# Revit family: 1322xxx Sparta 900 LED 0-10V (UL)
name_source: partatom
category: Lighting Fixtures
revit_build: Autodesk Revit 2018 (Build: 20170223_1515(x64)
units: mm (PartAtom-declared; Revit-internal decimal feet)

## family parameters
Always vertical = Yes
Cut with Voids When Loaded = No
Host = Wall
Light Source = Yes
OmniClass Number = 23.80.70.00
OmniClass Title = Lighting
Part Type = Normal
Room Calculation Point = No
Round Connector Dimension = Use Diameter
Shared = No

## types (1)
- Astro Sparta 900 LED 0-10V
    ADA compliant = Yes
    Color Filter = 16777215
    Dimmable = Yes
    Dimming Lamp Color Temperature Shift = <None>
    Dimming Method = 0-10V
    Driver Included = Yes
    Driver Required = No
    Efficacy (lm/w) = 99
    Electrical Class = 1
    Lamp = LED
    Light Source Fixed = Yes
    Location / IP Rating = Damp
    Main Finish = Polished Chrome
    Main Material = Metal - Aluminium
    Manufacturer = Astro Lighting Ltd
    Manufacturer URL - Europe and Rest of World = www.astrolighting.com
    Manufacturer URL - North America = us.astrolighting.com
    Photometric Web File = 1322010_Sparta 900 LED 0-10V _Photometry_IES_Iss. 01.IES
    Power (Watts) = 10.4
    Product CCT = 3000K
    Product CRI = 80
    Product Dimensions (MM) = 900x33x80
    Product Location = Bathroom
    Product Name = Sparta 900 LED 0-10V
    Product SKU = 1322010
    Product URL = https://us.astrolighting.com
    Product Weight (KG) = 1.53
    Tilt Angle = 0.00°
    URL = www.astrolighting.com

## geometry (parser evidence)
native form markers: Sweep x1
no freeform markers — native parametric forms only
